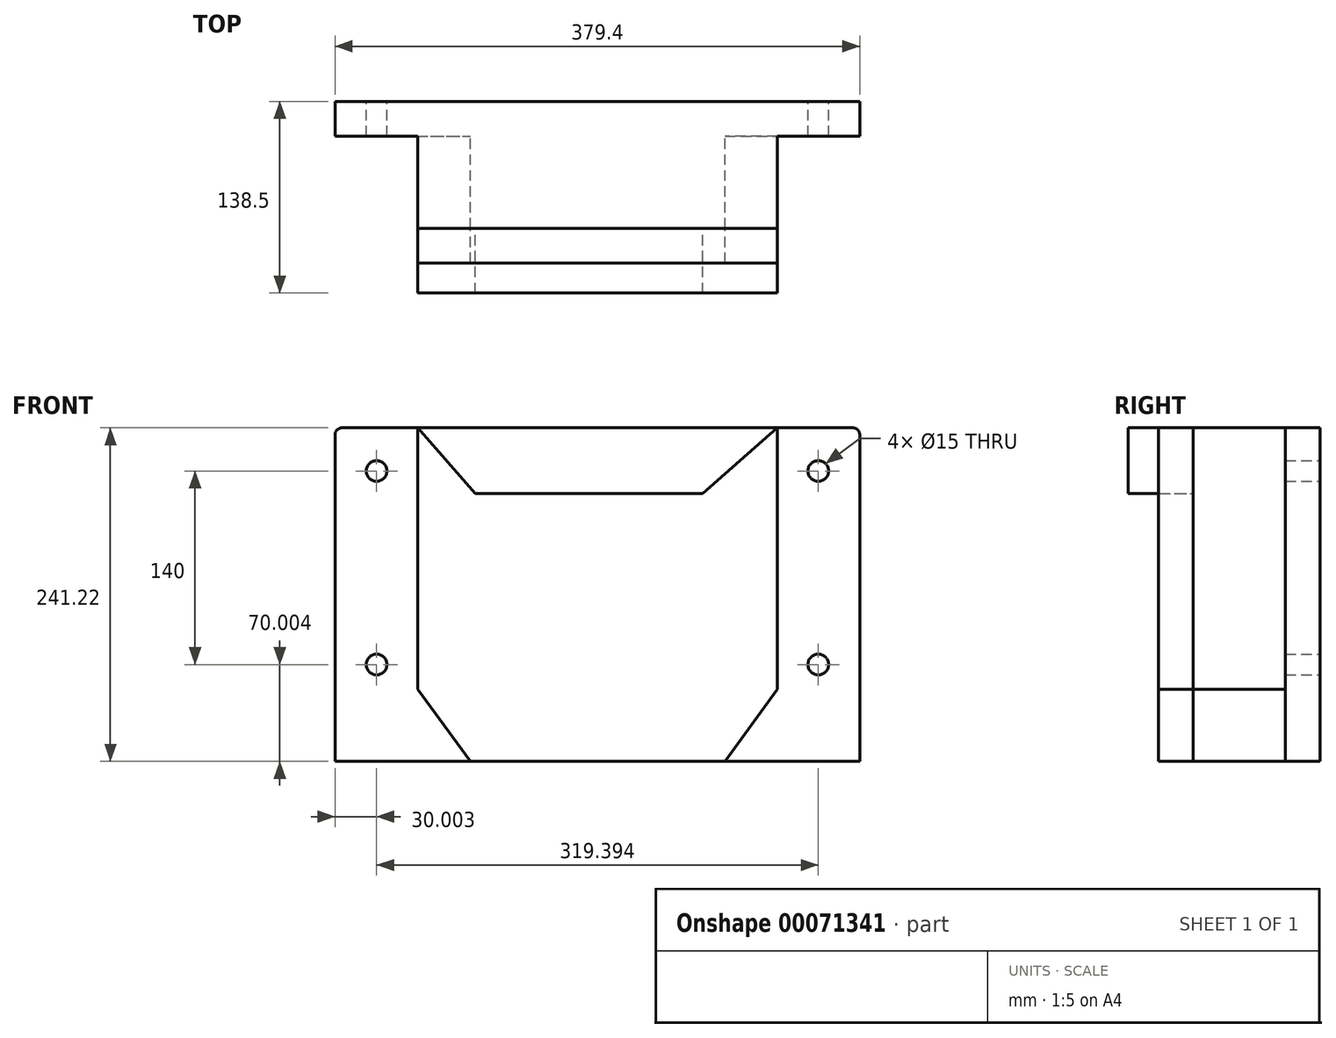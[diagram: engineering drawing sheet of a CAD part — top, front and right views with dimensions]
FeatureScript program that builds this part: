
annotation { "Feature Type Name" : "Feature", "Feature Type Description" : "" }
export const myFeature = defineFeature(function(context is Context, id is Id, definition is map)
    precondition{}
    {
        {
            var Q0;
            Q0=qCreatedBy(makeId("Front.planeOp"),FACE);
            var sketch = newSketch(context, id + "F0", { "sketchPlane" : qUnion([Q0])});
            skLineSegment(sketch, "E0.bottom", {"start": v(129.7, -77.58) * mm, "end": v(-129.7, -77.58) * mm});
            skLineSegment(sketch, "E0.top", {"start": v(129.7, 77.58) * mm, "end": v(-129.7, 77.58) * mm});
            skLineSegment(sketch, "E0.left", {"start": v(129.7, -77.58) * mm, "end": v(129.7, 77.58) * mm});
            skLineSegment(sketch, "E0.right", {"start": v(-129.7, -77.58) * mm, "end": v(-129.7, 77.58) * mm});
            skPoint(sketch, "E0.middle", {"position": v(0, 0) * mm});
            skLineSegment(sketch, "E1.left", {"start": v(-129.7, -77.58) * mm, "end": v(-129.7, -123.64) * mm});
            skLineSegment(sketch, "E1.right", {"start": v(129.7, -77.58) * mm, "end": v(129.7, -123.64) * mm});
            skLineSegment(sketch, "E2.top", {"start": v(-189.7, -163.64) * mm, "end": v(189.7, -163.64) * mm});
            skLineSegment(sketch, "E2.left", {"start": v(-189.7, -123.64) * mm, "end": v(-189.7, -163.64) * mm});
            skLineSegment(sketch, "E2.right", {"start": v(189.7, -123.64) * mm, "end": v(189.7, -163.64) * mm});
            skLineSegment(sketch, "E3.bottom", {"start": v(-129.7, 77.58) * mm, "end": v(-184.7, 77.58) * mm});
            skLineSegment(sketch, "E3.top", {"start": v(-129.7, -163.64) * mm, "end": v(-189.7, -163.64) * mm});
            skLineSegment(sketch, "E3.left", {"start": v(-129.7, 77.58) * mm, "end": v(-129.7, -163.64) * mm});
            skLineSegment(sketch, "E3.right", {"start": v(-189.7, 72.58) * mm, "end": v(-189.7, -163.64) * mm});
            skLineSegment(sketch, "E4.bottom", {"start": v(129.7, 77.58) * mm, "end": v(184.7, 77.58) * mm});
            skLineSegment(sketch, "E4.top", {"start": v(129.7, -163.64) * mm, "end": v(189.7, -163.64) * mm});
            skLineSegment(sketch, "E4.left", {"start": v(129.7, 77.58) * mm, "end": v(129.7, -163.64) * mm});
            skLineSegment(sketch, "E4.right", {"start": v(189.7, 72.58) * mm, "end": v(189.7, -163.64) * mm});
            skPoint(sketch, "E5.visualSharp", {"position": v(-189.7, 77.58) * mm});
            skArc(sketch, "E5.filletArc", {"start": v(-184.7, 77.58) * mm, "mid": v(-188.23, 76.11) * mm, "end": v(-189.7, 72.58) * mm});
            skPoint(sketch, "E6.visualSharp", {"position": v(189.7, 77.58) * mm});
            skArc(sketch, "E6.filletArc", {"start": v(189.7, 72.58) * mm, "mid": v(188.23, 76.11) * mm, "end": v(184.7, 77.58) * mm});
            skCircle(sketch, "E7", {"center": v(-159.7, 46.36) * mm, "radius": 7.5 * mm});
            skCircle(sketch, "E8", {"center": v(-159.7, -93.64) * mm, "radius": 7.5 * mm});
            skCircle(sketch, "E9.MirrorC", {"center": v(159.7, 46.36) * mm, "radius": 7.5 * mm});
            skCircle(sketch, "E10.MirrorC", {"center": v(159.7, -93.64) * mm, "radius": 7.5 * mm});
            skPoint(sketch, "E11.left.end.orphan", {"position": v(70.53, 27.92) * mm});
            skPoint(sketch, "E11.left.start.orphan", {"position": v(70.53, -27.92) * mm});
            skPoint(sketch, "E11.right.end.orphan", {"position": v(-70.53, 27.92) * mm});
            skPoint(sketch, "E11.right.start.orphan", {"position": v(-70.53, -27.92) * mm});
            skArc(sketch, "E12", {"start": v(-76.93, 77.58) * mm, "mid": v(0, 0.65) * mm, "end": v(76.93, 77.58) * mm});
            skSolve(sketch);
        }
        {
            var Q0;
            Q0 = qSketchRegion(id + "F0", true);
            extrude(context, id + "F1", {"entities" : qUnion([Q0]), "depth" : 25 * mm});
        }
        {
            var Q0;
            Q0=makeQuery(id+"F1.opExtrude","CAP_FACE",FACE,{"disambiguationData":[OSD([sQuery(id+"F0.wireOp",EDGE,"E0.top"),sQuery(id+"F0.wireOp",EDGE,"E2.top"),sQuery(id+"F0.wireOp",EDGE,"E3.bottom"),sQuery(id+"F0.wireOp",EDGE,"E3.top"),sQuery(id+"F0.wireOp",EDGE,"E3.right"),sQuery(id+"F0.wireOp",EDGE,"E4.bottom"),sQuery(id+"F0.wireOp",EDGE,"E4.top"),sQuery(id+"F0.wireOp",EDGE,"E4.right"),sQuery(id+"F0.wireOp",EDGE,"E5.filletArc"),sQuery(id+"F0.wireOp",EDGE,"E6.filletArc"),sQuery(id+"F0.wireOp",EDGE,"E7"),sQuery(id+"F0.wireOp",EDGE,"E8"),sQuery(id+"F0.wireOp",EDGE,"E9.MirrorC"),sQuery(id+"F0.wireOp",EDGE,"E10.MirrorC")])],"isStart":false});
            var sketch = newSketch(context, id + "F2", { "sketchPlane" : qUnion([Q0])});
            skLineSegment(sketch, "E13.bottom", {"start": v(-130.06, 77.58) * mm, "end": v(130.12, 77.58) * mm});
            skLineSegment(sketch, "E13.top", {"start": v(-91.96, -163.64) * mm, "end": v(92.24, -163.64) * mm});
            skLineSegment(sketch, "E14", {"start": v(-130.06, -111.45) * mm, "end": v(130.12, -111.45) * mm});
            skLineSegment(sketch, "E15", {"start": v(-130.06, -111.45) * mm, "end": v(-91.96, -163.64) * mm});
            skLineSegment(sketch, "E16", {"start": v(130.12, -111.45) * mm, "end": v(92.24, -163.64) * mm});
            skLineSegment(sketch, "E17", {"start": v(-130.06, 77.58) * mm, "end": v(-130.06, -111.45) * mm});
            skLineSegment(sketch, "E18", {"start": v(130.12, 77.58) * mm, "end": v(130.12, -111.45) * mm});
            skSolve(sketch);
        }
        {
            var Q0;
            Q0=makeQuery(id+"F2.imprint","IMPRINT",FACE,{"disambiguationData":[TD([[makeQuery(id+"F2.imprint","IMPRINT",EDGE,{"derivedFrom":sQuery(id+"F2.wireOp",EDGE,"E13.bottom")}),1.0]])]});
            extrude(context, id + "F3", {"entities" : qUnion([Q0]), "operationType" : NewBodyOperationType.ADD, "depth" : 42.5 * mm});
        }
        {
            var Q0;
            Q0 = qSketchRegion(id + "F2", true);
            extrude(context, id + "F4", {"entities" : qUnion([Q0]), "operationType" : NewBodyOperationType.ADD, "depth" : 66.75 * mm});
        }
        {
            var Q0;
            Q0=makeQuery(id+"F4.opExtrude","CAP_FACE",FACE,{"disambiguationData":[OSD([sQuery(id+"F2.wireOp",EDGE,"E13.bottom"),sQuery(id+"F2.wireOp",EDGE,"E13.top"),sQuery(id+"F2.wireOp",EDGE,"E15"),sQuery(id+"F2.wireOp",EDGE,"E16"),sQuery(id+"F2.wireOp",EDGE,"E17"),sQuery(id+"F2.wireOp",EDGE,"E18")])],"isStart":false});
            var sketch = newSketch(context, id + "F5", { "sketchPlane" : qUnion([Q0])});
            skLineSegment(sketch, "E19", {"start": v(-130.06, 77.58) * mm, "end": v(-88.41, 30.1) * mm});
            skLineSegment(sketch, "E20", {"start": v(130.12, 77.58) * mm, "end": v(76, 30.1) * mm});
            skLineSegment(sketch, "E21", {"start": v(76, 30.1) * mm, "end": v(130.12, 30.1) * mm});
            skLineSegment(sketch, "E22", {"start": v(-88.41, 30.1) * mm, "end": v(-130.06, 30.1) * mm});
            skLineSegment(sketch, "E23", {"start": v(-88.41, 30.1) * mm, "end": v(76, 30.1) * mm});
            skSolve(sketch);
        }
        {
            var Q0;
            Q0 = qSketchRegion(id + "F5", true);
            var Q1;
            Q1=makeQuery(id+"F5.imprint","IMPRINT",FACE,{"disambiguationData":[TD([[makeQuery(id+"F5.imprint","IMPRINT",EDGE,{"derivedFrom":sQuery(id+"F5.wireOp",EDGE,"E19")}),1.0]])]});
            extrude(context, id + "F6", {"entities" : qUnion([Q0, Q1]), "depth" : 46.75 * mm});
        }
        {
            var Q0;
            Q0=makeQuery(id+"F4.opExtrude","CAP_FACE",FACE,{"disambiguationData":[OSD([sQuery(id+"F2.wireOp",EDGE,"E13.bottom"),sQuery(id+"F2.wireOp",EDGE,"E13.top"),sQuery(id+"F2.wireOp",EDGE,"E15"),sQuery(id+"F2.wireOp",EDGE,"E16"),sQuery(id+"F2.wireOp",EDGE,"E17"),sQuery(id+"F2.wireOp",EDGE,"E18")])],"isStart":false});
            var sketch = newSketch(context, id + "F7", { "sketchPlane" : qUnion([Q0])});
            skLineSegment(sketch, "E24", {"start": v(-104.9, 73.11) * mm, "end": v(-91.96, -163.64) * mm});
            skLineSegment(sketch, "E25", {"start": v(59.3, 73.8) * mm, "end": v(92.24, -163.64) * mm});
            skLineSegment(sketch, "E26", {"start": v(-91.96, -163.64) * mm, "end": v(92.24, -163.64) * mm});
            skSolve(sketch);
        }
        {
            var Q0;
            Q0 = qSketchRegion(id + "F7", true);
            var Q1;
            Q1=makeQuery(id+"F7.imprint","IMPRINT",FACE,{"disambiguationData":[TD([[makeQuery(id+"F7.imprint","IMPRINT",EDGE,{"derivedFrom":sQuery(id+"F7.wireOp",EDGE,"E26")}),1.0]])]});
            extrude(context, id + "F8", {"entities" : qUnion([Q0, Q1]), "depth" : 25 * mm});
        }
    });
